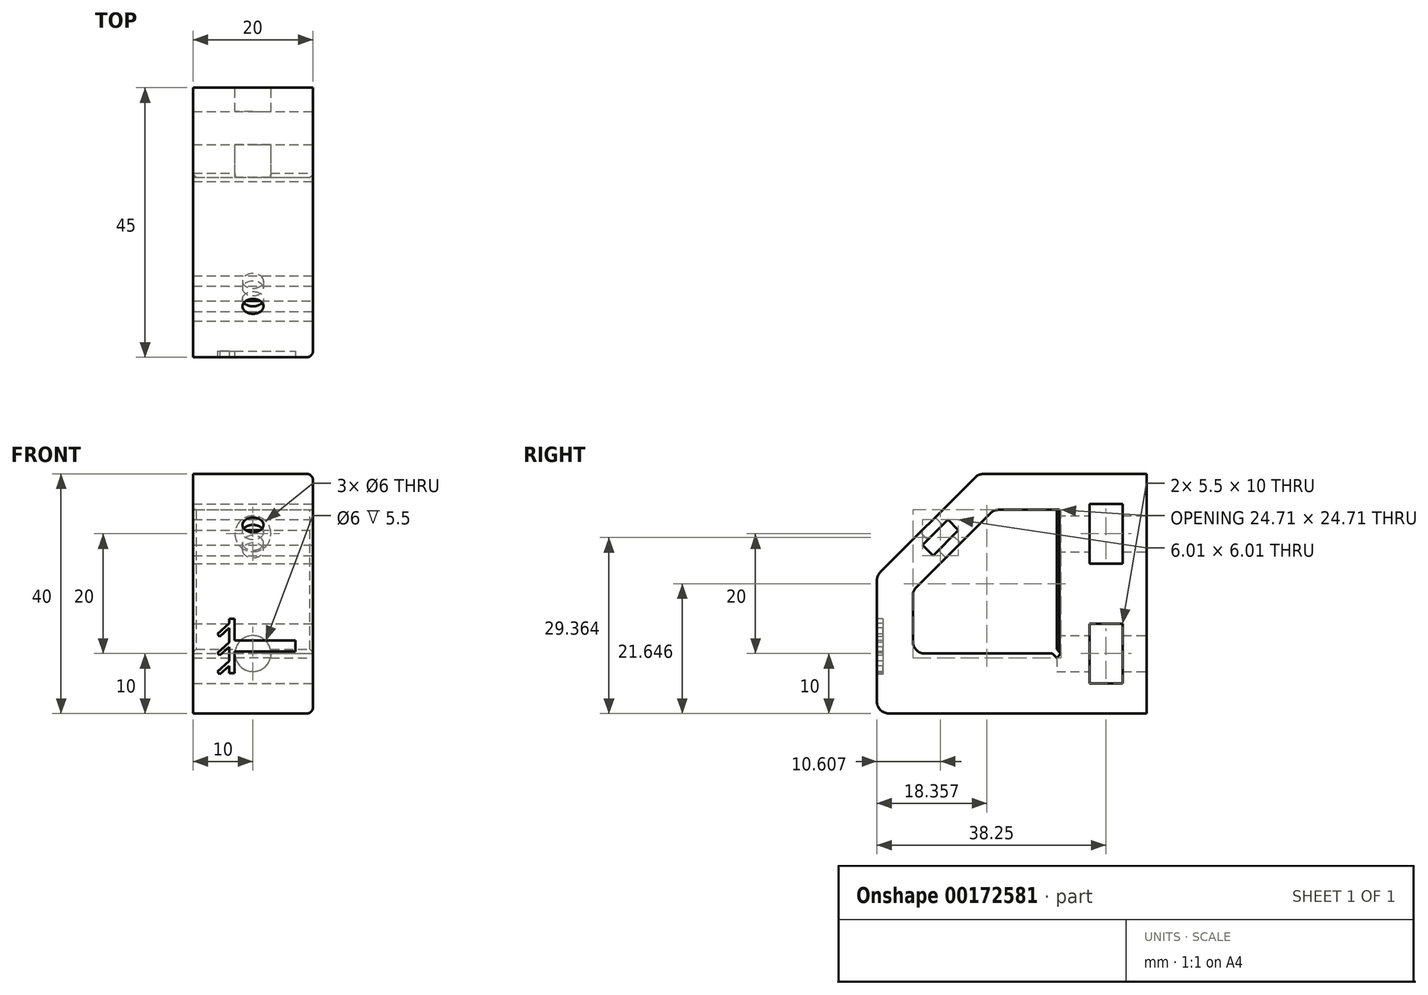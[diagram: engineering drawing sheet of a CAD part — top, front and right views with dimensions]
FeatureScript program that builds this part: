
annotation { "Feature Type Name" : "Feature", "Feature Type Description" : "" }
export const myFeature = defineFeature(function(context is Context, id is Id, definition is map)
    precondition{}
    {
        {
            var Q0;
            Q0=qCreatedBy(makeId("Front.planeOp"),FACE);
            var sketch = newSketch(context, id + "F0", { "sketchPlane" : qUnion([Q0])});
            skLineSegment(sketch, "E0.bottom", {"start": v(0, 0) * mm, "end": v(20, 0) * mm});
            skLineSegment(sketch, "E0.top", {"start": v(0, 40) * mm, "end": v(20, 40) * mm});
            skLineSegment(sketch, "E0.left", {"start": v(0, 0) * mm, "end": v(0, 40) * mm});
            skLineSegment(sketch, "E0.right", {"start": v(20, 0) * mm, "end": v(20, 40) * mm});
            skSolve(sketch);
        }
        {
            var Q0;
            Q0=qSketchRegion(id+"F0",true);
            extrude(context, id + "F1", {"entities" : qUnion([Q0]), "depth" : 15 * mm});
        }
        {
            var Q0;
            Q0=makeQuery(id+"F1.opExtrude","SWEPT_FACE",FACE,{"disambiguationData":[OSD([sQuery(id+"F0.wireOp",EDGE,"E0.right")])]});
            var sketch = newSketch(context, id + "F2", { "sketchPlane" : qUnion([Q0])});
            skLineSegment(sketch, "E1", {"start": v(-15, 0) * mm, "end": v(-45, 0) * mm});
            skLineSegment(sketch, "E2", {"start": v(-45, 0) * mm, "end": v(-45, 23) * mm});
            skLineSegment(sketch, "E3", {"start": v(-39, 10) * mm, "end": v(-15, 10) * mm});
            skLineSegment(sketch, "E4", {"start": v(-15, 10) * mm, "end": v(-15, 0) * mm});
            skLineSegment(sketch, "E5", {"start": v(-15, 40) * mm, "end": v(-28, 40) * mm});
            skLineSegment(sketch, "E6", {"start": v(-28, 40) * mm, "end": v(-45, 23) * mm});
            skLineSegment(sketch, "E7", {"start": v(-15, 34) * mm, "end": v(-25.51, 34) * mm});
            skLineSegment(sketch, "E8", {"start": v(-25.51, 34) * mm, "end": v(-39, 20.51) * mm});
            skLineSegment(sketch, "E9", {"start": v(-39, 20.51) * mm, "end": v(-39, 10) * mm});
            skSolve(sketch);
        }
        {
            var Q0;
            Q0=qSketchRegion(id+"F2",true);
            var Q1;
            Q1=makeQuery(id+"F2.imprint","IMPRINT",FACE,{"disambiguationData":[TD([[makeQuery(id+"F2.imprint","IMPRINT",EDGE,{"derivedFrom":sQuery(id+"F2.wireOp",EDGE,"E1")}),-1.0]])]});
            var Q2;
            Q2=makeQuery(id+"F1.opExtrude","SWEPT_FACE",FACE,{"disambiguationData":[OSD([sQuery(id+"F0.wireOp",EDGE,"E0.left")])]});
            extrude(context, id + "F3", {"entities" : qUnion([Q0, Q1]), "operationType" : NewBodyOperationType.ADD, "endBound" : BoundingType.UP_TO_SURFACE, "oppositeDirection" : true, "endBoundEntityFace" : qUnion([Q2]), "depth" : 25 * mm});
        }
        {
            var Q0;
            Q0=makeQuery(id+"F1.opExtrude","CAP_FACE",FACE,{"disambiguationData":[OSD([sQuery(id+"F0.wireOp",EDGE,"E0.bottom"),sQuery(id+"F0.wireOp",EDGE,"E0.top"),sQuery(id+"F0.wireOp",EDGE,"E0.left"),sQuery(id+"F0.wireOp",EDGE,"E0.right")])],"isStart":true});
            var sketch = newSketch(context, id + "F4", { "sketchPlane" : qUnion([Q0])});
            skCircle(sketch, "E10", {"center": v(-10, 30) * mm, "radius": 3 * mm});
            skPoint(sketch, "E10.centerSnap0", {"position": v(-10, 40) * mm});
            skCircle(sketch, "E11", {"center": v(-10, 10) * mm, "radius": 3 * mm});
            skSolve(sketch);
        }
        {
            var Q0;
            Q0=qSketchRegion(id+"F4",true);
            var Q1;
            Q1=makeQuery(id+"F1.opExtrude","CAP_FACE",FACE,{"disambiguationData":[OSD([sQuery(id+"F0.wireOp",EDGE,"E0.bottom"),sQuery(id+"F0.wireOp",EDGE,"E0.top"),sQuery(id+"F0.wireOp",EDGE,"E0.left"),sQuery(id+"F0.wireOp",EDGE,"E0.right")])],"isStart":false});
            extrude(context, id + "F5", {"entities" : qUnion([Q0]), "operationType" : NewBodyOperationType.REMOVE, "endBound" : BoundingType.UP_TO_SURFACE, "oppositeDirection" : true, "endBoundEntityFace" : qUnion([Q1]), "depth" : 25 * mm});
        }
        {
            var Q0;
            {var subQ0=sQuery(id+"F0.wireOp",EDGE,"E0.right");Q0=makeQuery(id+"F3.boolean.opBoolean","MERGE",FACE,{"derivedFrom":[makeQuery(id+"F1.opExtrude","SWEPT_FACE",FACE,{"disambiguationData":[OSD([subQ0])]}),makeQuery(id+"F3.opExtrude","CAP_FACE",FACE,{"disambiguationData":[OSD([subQ0,sQuery(id+"F2.wireOp",EDGE,"E1"),sQuery(id+"F2.wireOp",EDGE,"E2"),sQuery(id+"F2.wireOp",EDGE,"oFBr16c8-0Q2X-FP0S-YIid-CgedbtGLqJMR"),sQuery(id+"F2.wireOp",EDGE,"evPOPMKi-VTVA-ff8v-8ZP8-QB7idNNDxLJc"),sQuery(id+"F2.wireOp",EDGE,"pkw4sknF-nVUN-RSqT-HF6s-BWwzk2YnTHOt"),sQuery(id+"F2.wireOp",EDGE,"E3"),sQuery(id+"F2.wireOp",EDGE,"E4")])],"isStart":true})]});}
            var sketch = newSketch(context, id + "F6", { "sketchPlane" : qUnion([Q0])});
            skLineSegment(sketch, "E12", {"start": v(-15.7, 10) * mm, "end": v(-15, 9.3) * mm});
            skLineSegment(sketch, "E13", {"start": v(-15, 9.3) * mm, "end": v(-14.29, 10) * mm});
            skLineSegment(sketch, "E14", {"start": v(-14.29, 10) * mm, "end": v(-15, 10.71) * mm});
            skSolve(sketch);
        }
        {
            var Q0;
            Q0=qSketchRegion(id+"F6",true);
            var Q1;
            {var subQ4=sQuery(id+"F6.wireOp",EDGE,"E12");Q1=makeQuery(id+"F6.imprint","IMPRINT",FACE,{"disambiguationData":[TD([[makeQuery(id+"F6.imprint","IMPRINT",EDGE,{"derivedFrom":subQ4}),1.0]])]});}
            extrude(context, id + "F7", {"entities" : qUnion([Q0, Q1]), "operationType" : NewBodyOperationType.REMOVE, "oppositeDirection" : true, "depth" : 25 * mm});
        }
        {
            var Q0;
            Q0=makeQuery(id+"F3.opExtrude","SWEPT_FACE",FACE,{"disambiguationData":[OSD([sQuery(id+"F2.wireOp",EDGE,"E6")])]});
            var sketch = newSketch(context, id + "F8", { "sketchPlane" : qUnion([Q0])});
            skCircle(sketch, "E15", {"center": v(10, -3.56) * mm, "radius": 1.75 * mm});
            skPoint(sketch, "E15.centerSnap0", {"position": v(10, -15.56) * mm});
            skSolve(sketch);
        }
        {
            var Q0;
            Q0=qSketchRegion(id+"F8",true);
            extrude(context, id + "F9", {"entities" : qUnion([Q0]), "operationType" : NewBodyOperationType.REMOVE, "endBound" : BoundingType.UP_TO_NEXT, "oppositeDirection" : true, "depth" : 25 * mm});
        }
        {
            var Q0;
            {var subQ0=sQuery(id+"F0.wireOp",EDGE,"E0.right");Q0=makeQuery(id+"F3.boolean.opBoolean","MERGE",FACE,{"derivedFrom":[makeQuery(id+"F1.opExtrude","SWEPT_FACE",FACE,{"disambiguationData":[OSD([subQ0])]}),makeQuery(id+"F3.opExtrude","CAP_FACE",FACE,{"disambiguationData":[OSD([subQ0,sQuery(id+"F2.wireOp",EDGE,"E1"),sQuery(id+"F2.wireOp",EDGE,"E2"),sQuery(id+"F2.wireOp",EDGE,"E3"),sQuery(id+"F2.wireOp",EDGE,"E4"),sQuery(id+"F2.wireOp",EDGE,"E5"),sQuery(id+"F2.wireOp",EDGE,"E6"),sQuery(id+"F2.wireOp",EDGE,"E7"),sQuery(id+"F2.wireOp",EDGE,"E8"),sQuery(id+"F2.wireOp",EDGE,"E9")])],"isStart":true})]});}
            var sketch = newSketch(context, id + "F10", { "sketchPlane" : qUnion([Q0])});
            skLineSegment(sketch, "E16", {"start": v(-37.4, 28.13) * mm, "end": v(-33.16, 32.37) * mm});
            skLineSegment(sketch, "E17", {"start": v(-33.16, 32.37) * mm, "end": v(-31.39, 30.6) * mm});
            skLineSegment(sketch, "E18", {"start": v(-31.39, 30.6) * mm, "end": v(-35.63, 26.36) * mm});
            skLineSegment(sketch, "E19", {"start": v(-35.63, 26.36) * mm, "end": v(-37.4, 28.13) * mm});
            skLineSegment(sketch, "E20", {"start": v(-35.28, 30.25) * mm, "end": v(-33.5, 28.48) * mm, "construction": true});
            skSolve(sketch);
        }
        {
            var Q0;
            Q0=qSketchRegion(id+"F10",true);
            extrude(context, id + "F11", {"entities" : qUnion([Q0]), "operationType" : NewBodyOperationType.REMOVE, "oppositeDirection" : true, "depth" : 25 * mm});
        }
        {
            var Q0;
            Q0=makeQuery(id+"F3.opExtrude","SWEPT_EDGE",EDGE,{"disambiguationData":[OSD([sQuery(id+"F2.wireOp",EDGE,"E2"),sQuery(id+"F2.wireOp",EDGE,"E6")])]});
            var Q1;
            Q1=makeQuery(id+"F3.opExtrude","SWEPT_EDGE",EDGE,{"disambiguationData":[OSD([sQuery(id+"F2.wireOp",EDGE,"E1"),sQuery(id+"F2.wireOp",EDGE,"E2")])]});
            var Q2;
            Q2=makeQuery(id+"F3.opExtrude","SWEPT_EDGE",EDGE,{"disambiguationData":[OSD([sQuery(id+"F2.wireOp",EDGE,"E5"),sQuery(id+"F2.wireOp",EDGE,"E6")])]});
            var Q3;
            Q3=makeQuery(id+"F3.opExtrude","SWEPT_EDGE",EDGE,{"disambiguationData":[OSD([sQuery(id+"F2.wireOp",EDGE,"E8"),sQuery(id+"F2.wireOp",EDGE,"E9")])]});
            var Q4;
            Q4=makeQuery(id+"F3.opExtrude","SWEPT_EDGE",EDGE,{"disambiguationData":[OSD([sQuery(id+"F2.wireOp",EDGE,"E7"),sQuery(id+"F2.wireOp",EDGE,"E8")])]});
            var Q5;
            Q5=makeQuery(id+"F3.opExtrude","SWEPT_EDGE",EDGE,{"disambiguationData":[OSD([sQuery(id+"F2.wireOp",EDGE,"E3"),sQuery(id+"F2.wireOp",EDGE,"E9")])]});
            var Q6;
            Q6=makeQuery(id+"F3.opExtrude","SWEPT_EDGE",EDGE,{"disambiguationData":[OSD([sQuery(id+"F0.wireOp",EDGE,"E0.right"),sQuery(id+"F2.wireOp",EDGE,"E7")])]});
            fillet(context, id + "F12", {"entities" : qUnion([Q0, Q1, Q2, Q3, Q4, Q5, Q6]), "radius" : 2 * mm, "tangentPropagation" : true, "allowEdgeOverflow" : false});
        }
        {
            var Q0;
            Q0=makeQuery(id+"F3.opExtrude","CAP_EDGE",EDGE,{"disambiguationData":[OSD([sQuery(id+"F2.wireOp",EDGE,"E6")])],"isStart":true});
            var Q1;
            Q1=makeQuery(id+"F3.opExtrude","TWEAK_EDGE",EDGE,{"derivedFrom":[makeQuery(id+"F1.opExtrude","SWEPT_FACE",FACE,{"disambiguationData":[OSD([sQuery(id+"F0.wireOp",EDGE,"E0.left")])]}),makeQuery(id+"F2.imprint","IMPRINT",EDGE,{"derivedFrom":sQuery(id+"F2.wireOp",EDGE,"E6")})]});
            fillet(context, id + "F13", {"entities" : qUnion([Q0, Q1]), "radius" : 1 * mm, "tangentPropagation" : true, "allowEdgeOverflow" : false});
        }
        {
            var Q0;
            {var subQ0=sQuery(id+"F0.wireOp",EDGE,"E0.right");Q0=makeQuery(id+"F3.boolean.opBoolean","MERGE",FACE,{"derivedFrom":[makeQuery(id+"F1.opExtrude","SWEPT_FACE",FACE,{"disambiguationData":[OSD([subQ0])]}),makeQuery(id+"F3.opExtrude","CAP_FACE",FACE,{"disambiguationData":[OSD([subQ0,sQuery(id+"F2.wireOp",EDGE,"E1"),sQuery(id+"F2.wireOp",EDGE,"E2"),sQuery(id+"F2.wireOp",EDGE,"E3"),sQuery(id+"F2.wireOp",EDGE,"E4"),sQuery(id+"F2.wireOp",EDGE,"E5"),sQuery(id+"F2.wireOp",EDGE,"E6"),sQuery(id+"F2.wireOp",EDGE,"E7"),sQuery(id+"F2.wireOp",EDGE,"E8"),sQuery(id+"F2.wireOp",EDGE,"E9")])],"isStart":true})]});}
            var sketch = newSketch(context, id + "F14", { "sketchPlane" : qUnion([Q0])});
            skLineSegment(sketch, "E21.bottom", {"start": v(-9.5, 35) * mm, "end": v(-4, 35) * mm});
            skLineSegment(sketch, "E21.top", {"start": v(-9.5, 25) * mm, "end": v(-4, 25) * mm});
            skLineSegment(sketch, "E21.left", {"start": v(-9.5, 35) * mm, "end": v(-9.5, 25) * mm});
            skLineSegment(sketch, "E21.right", {"start": v(-4, 35) * mm, "end": v(-4, 25) * mm});
            skLineSegment(sketch, "E22.bottom", {"start": v(-9.5, 15) * mm, "end": v(-4, 15) * mm});
            skLineSegment(sketch, "E22.top", {"start": v(-9.5, 5) * mm, "end": v(-4, 5) * mm});
            skLineSegment(sketch, "E22.left", {"start": v(-9.5, 15) * mm, "end": v(-9.5, 5) * mm});
            skLineSegment(sketch, "E22.right", {"start": v(-4, 15) * mm, "end": v(-4, 5) * mm});
            skSolve(sketch);
        }
        {
            var Q0;
            Q0=qSketchRegion(id+"F14",true);
            extrude(context, id + "F15", {"entities" : qUnion([Q0]), "operationType" : NewBodyOperationType.REMOVE, "oppositeDirection" : true, "depth" : 25 * mm});
        }
        {
            var Q0;
            Q0=makeQuery(id+"F3.opExtrude","SWEPT_FACE",FACE,{"disambiguationData":[OSD([sQuery(id+"F2.wireOp",EDGE,"E2")])]});
            var sketch = newSketch(context, id + "F16", { "sketchPlane" : qUnion([Q0])});
            skLineSegment(sketch, "E23.bottom", {"start": v(6.02, 15.8) * mm, "end": v(6.9, 15.8) * mm});
            skLineSegment(sketch, "E23.top", {"start": v(6.02, 6.72) * mm, "end": v(6.9, 6.72) * mm});
            skLineSegment(sketch, "E23.left", {"start": v(6.02, 15.8) * mm, "end": v(6.02, 6.72) * mm});
            skLineSegment(sketch, "E23.right", {"start": v(6.9, 15.8) * mm, "end": v(6.9, 6.72) * mm});
            skLineSegment(sketch, "E24.bottom", {"start": v(6.9, 12.18) * mm, "end": v(17.1, 12.18) * mm});
            skLineSegment(sketch, "E24.top", {"start": v(6.9, 10.33) * mm, "end": v(17.1, 10.33) * mm});
            skLineSegment(sketch, "E24.left", {"start": v(6.9, 12.18) * mm, "end": v(6.9, 10.33) * mm});
            skLineSegment(sketch, "E24.right", {"start": v(17.1, 12.18) * mm, "end": v(17.1, 10.33) * mm});
            skLineSegment(sketch, "E25", {"start": v(6.02, 15.04) * mm, "end": v(4.08, 13.26) * mm});
            skLineSegment(sketch, "E26", {"start": v(4.08, 13.26) * mm, "end": v(4.46, 12.84) * mm});
            skLineSegment(sketch, "E27", {"start": v(4.46, 12.84) * mm, "end": v(6.02, 14.27) * mm});
            skLineSegment(sketch, "E28.1.0.0", {"start": v(4.46, 9.7) * mm, "end": v(6.02, 11.12) * mm});
            skLineSegment(sketch, "E28.1.0.1", {"start": v(6.02, 11.89) * mm, "end": v(4.08, 10.1) * mm});
            skLineSegment(sketch, "E28.1.0.2", {"start": v(4.08, 10.1) * mm, "end": v(4.46, 9.7) * mm});
            skLineSegment(sketch, "E28.2.0.0", {"start": v(4.46, 6.54) * mm, "end": v(6.02, 7.96) * mm});
            skLineSegment(sketch, "E28.2.0.1", {"start": v(6.02, 8.73) * mm, "end": v(4.08, 6.95) * mm});
            skLineSegment(sketch, "E28.2.0.2", {"start": v(4.08, 6.95) * mm, "end": v(4.46, 6.54) * mm});
            skLineSegment(sketch, "E28.direction1", {"start": v(4.46, 12.84) * mm, "end": v(4.46, 9.7) * mm, "construction": true});
            skSolve(sketch);
        }
        {
            var Q0;
            Q0 = qSketchRegion(id + "F16", true);
            extrude(context, id + "F17", {"entities" : qUnion([Q0]), "operationType" : NewBodyOperationType.REMOVE, "oppositeDirection" : true, "depth" : 1 * mm});
        }
        {
            var Q0;
            Q0=makeQuery(id+"F1.opExtrude","CAP_EDGE",EDGE,{"disambiguationData":[OSD([sQuery(id+"F0.wireOp",EDGE,"E0.right")])],"isStart":false});
            var Q1;
            Q1=makeQuery(id+"F1.opExtrude","CAP_EDGE",EDGE,{"disambiguationData":[OSD([sQuery(id+"F0.wireOp",EDGE,"E0.left")])],"isStart":false});
            chamfer(context, id + "F18", {"entities" : qUnion([Q0, Q1]), "width" : 0.5 * mm, "tangentPropagation" : true});
        }
    });
